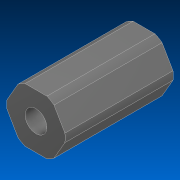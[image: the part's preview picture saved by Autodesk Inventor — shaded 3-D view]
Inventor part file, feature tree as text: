
AUTODESK INVENTOR PART (.ipt)
format: ipt  version: 2022.2 (Build 262287000, 287)  size: 130,048 bytes
history: native  units: in
note: dims shown in document units (in); Inventor stores cm internally (conversion verified against a paired STEP export)
features: extrude x1, sketch x1, other x1
ambient origin geometry x8: Origin, YZ Plane, XZ Plane, XY Plane, X Axis, Y Axis, Z Axis, Center Point
bodies: Solid1 (feature_tree)
feature tree (3):
  extrude  "Extrusion1"  TaperAngle=0.0deg  [1 undecoded]
  sketch  "Sketch1"  dims[d0=35.0in d1=0.0in]
  other  "Cut-Extrude2"
note: 1 required parameter value undecoded (feature->parameter linkage not recoverable at this tier; creation-order binding heuristic only, values carry confidence <= 0.55)
